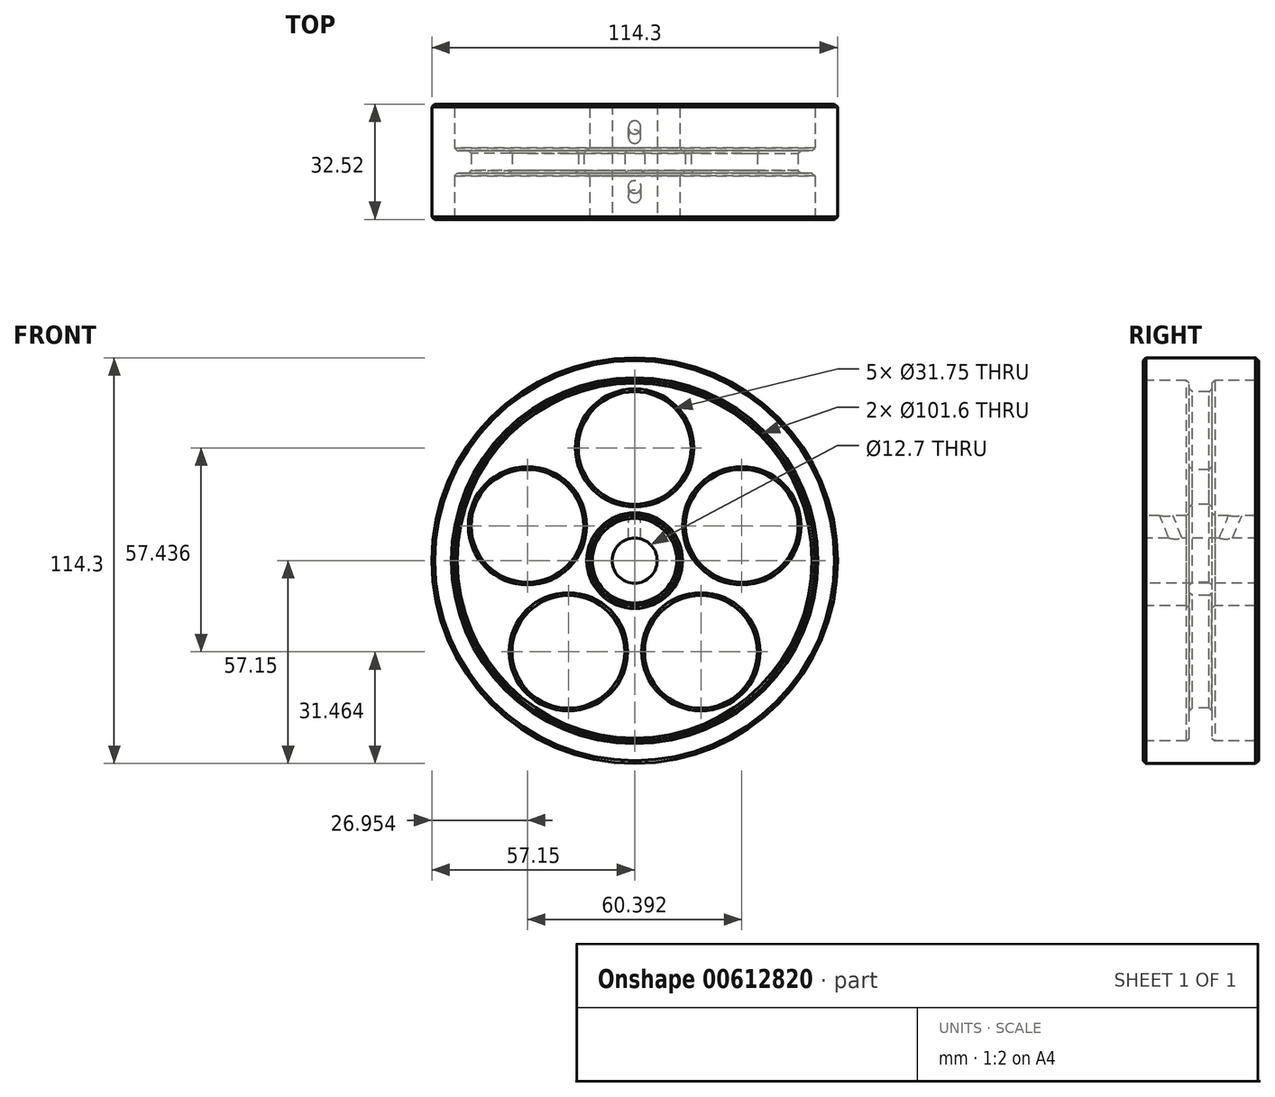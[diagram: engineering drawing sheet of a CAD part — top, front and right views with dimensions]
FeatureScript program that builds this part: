
annotation { "Feature Type Name" : "Feature", "Feature Type Description" : "" }
export const myFeature = defineFeature(function(context is Context, id is Id, definition is map)
    precondition{}
    {
        {
            var Q0;
            Q0=qCreatedBy(makeId("Right.planeOp"),FACE);
            var sketch = newSketch(context, id + "F0", { "sketchPlane" : qUnion([Q0])});
            skLineSegment(sketch, "E0", {"start": v(-16.26, 6.35) * mm, "end": v(-16.26, 12.7) * mm});
            skLineSegment(sketch, "E1", {"start": v(-16.26, 12.7) * mm, "end": v(-3.17, 12.7) * mm});
            skLineSegment(sketch, "E2", {"start": v(-3.17, 12.7) * mm, "end": v(-3.18, 50.8) * mm});
            skLineSegment(sketch, "E3", {"start": v(-3.18, 50.8) * mm, "end": v(-16.26, 50.8) * mm});
            skLineSegment(sketch, "E4", {"start": v(-16.26, 50.8) * mm, "end": v(-16.26, 57.15) * mm});
            skLineSegment(sketch, "E5", {"start": v(-16.26, 57.15) * mm, "end": v(16.26, 57.15) * mm});
            skLineSegment(sketch, "E6", {"start": v(16.26, 57.15) * mm, "end": v(16.26, 50.8) * mm});
            skLineSegment(sketch, "E7", {"start": v(16.26, 50.8) * mm, "end": v(3.17, 50.8) * mm});
            skLineSegment(sketch, "E8", {"start": v(3.17, 50.8) * mm, "end": v(3.18, 12.7) * mm});
            skLineSegment(sketch, "E9", {"start": v(3.18, 12.7) * mm, "end": v(16.26, 12.7) * mm});
            skLineSegment(sketch, "E10", {"start": v(16.26, 12.7) * mm, "end": v(16.26, 6.35) * mm});
            skLineSegment(sketch, "E11", {"start": v(16.26, 6.35) * mm, "end": v(-16.26, 6.35) * mm});
            skLineSegment(sketch, "E12", {"start": v(-16.39, 0) * mm, "end": v(18.55, 0) * mm, "construction": true});
            skPoint(sketch, "E13", {"position": v(0, 57.15) * mm});
            skPoint(sketch, "E14", {"position": v(-9.72, 12.7) * mm});
            skPoint(sketch, "E15", {"position": v(9.72, 12.7) * mm});
            skSolve(sketch);
        }
        {
            var Q0;
            Q0=qSketchRegion(id+"F0",true);
            var Q1;
            Q1=sQuery(id+"F0.wireOp",EDGE,"E12");
            revolve(context, id + "F1", {"entities" : qUnion([Q0]), "axis" : qUnion([Q1]), "revolveType" : RevolveType.FULL});
        }
        {
            var Q0;
            Q0=qCreatedBy(makeId("Front.planeOp"),FACE);
            var sketch = newSketch(context, id + "F2", { "sketchPlane" : qUnion([Q0])});
            skCircle(sketch, "E16", {"center": v(0, 31.75) * mm, "radius": 15.88 * mm});
            skCircle(sketch, "E17.1.0", {"center": v(-30.2, 9.81) * mm, "radius": 15.88 * mm});
            skCircle(sketch, "E17.2.0", {"center": v(-18.66, -25.69) * mm, "radius": 15.88 * mm});
            skCircle(sketch, "E17.3.0", {"center": v(18.66, -25.69) * mm, "radius": 15.88 * mm});
            skCircle(sketch, "E17.4.0", {"center": v(30.2, 9.81) * mm, "radius": 15.88 * mm});
            skPoint(sketch, "E17.center", {"position": v(0, 0) * mm});
            skCircle(sketch, "E18", {"center": v(0, 0) * mm, "radius": 31.75 * mm, "construction": true});
            skSolve(sketch);
        }
        {
            var Q0;
            Q0=qSketchRegion(id+"F2",true);
            extrude(context, id + "F3", {"entities" : qUnion([Q0]), "operationType" : NewBodyOperationType.REMOVE, "oppositeDirection" : true, "depth" : 50.8 * mm, "symmetric" : true});
        }
        {
            var Q0;
            Q0=qCreatedBy(makeId("Top.planeOp"),FACE);
            var sketch = newSketch(context, id + "F4", { "sketchPlane" : qUnion([Q0])});
            skLineSegment(sketch, "E19", {"start": v(-62.2, -50.8) * mm, "end": v(72.14, -50.8) * mm, "construction": true});
            skLineSegment(sketch, "E20", {"start": v(-62.2, 50.8) * mm, "end": v(72.14, 50.8) * mm, "construction": true});
            skSolve(sketch);
        }
        {
            var Q0;
            Q0=sQuery(id+"F4.wireOp",EDGE,"E19");
            cPlane(context, id + "F5", {"entities" : qUnion([Q0]), "cplaneType" : CPlaneType.LINE_ANGLE, "offset" : 152.4 * mm, "angle" : 292.5 * degree, "width" : 152.4 * mm, "height" : 152.4 * mm});
        }
        {
            var Q0;
            Q0=sQuery(id+"F4.wireOp",EDGE,"E20");
            cPlane(context, id + "F6", {"entities" : qUnion([Q0]), "cplaneType" : CPlaneType.LINE_ANGLE, "offset" : 152.4 * mm, "angle" : 67.5 * degree, "width" : 152.4 * mm, "height" : 152.4 * mm});
        }
        {
            var Q0;
            Q0=qCreatedBy(id+"F5.planeOp",FACE);
            var sketch = newSketch(context, id + "F7", { "sketchPlane" : qUnion([Q0])});
            skCircle(sketch, "E21", {"center": v(0, 4.12) * mm, "radius": 1.73 * mm});
            skSolve(sketch);
        }
        {
            var Q0;
            Q0=qSketchRegion(id+"F7",true);
            var Q1;
            Q1=makeQuery(id+"F1.opRevolve","SWEPT_FACE",FACE,{"disambiguationData":[OSD([sQuery(id+"F0.wireOp",EDGE,"E11")])]});
            extrude(context, id + "F8", {"entities" : qUnion([Q0]), "operationType" : NewBodyOperationType.REMOVE, "endBound" : BoundingType.UP_TO_SURFACE, "endBoundEntityFace" : qUnion([Q1]), "depth" : 25.4 * mm});
        }
        {
            var Q0;
            Q0=qCreatedBy(id+"F6.planeOp",FACE);
            var sketch = newSketch(context, id + "F9", { "sketchPlane" : qUnion([Q0])});
            skCircle(sketch, "E22", {"center": v(0, 4.12) * mm, "radius": 1.73 * mm});
            skSolve(sketch);
        }
        {
            var Q0;
            Q0=qSketchRegion(id+"F9",true);
            var Q1;
            Q1=makeQuery(id+"F1.opRevolve","SWEPT_FACE",FACE,{"disambiguationData":[OSD([sQuery(id+"F0.wireOp",EDGE,"E11")])]});
            extrude(context, id + "F10", {"entities" : qUnion([Q0]), "operationType" : NewBodyOperationType.REMOVE, "endBound" : BoundingType.UP_TO_SURFACE, "oppositeDirection" : true, "endBoundEntityFace" : qUnion([Q1]), "depth" : 25.4 * mm});
        }
        {
            var Q0;
            Q0=makeQuery(id+"F1.opRevolve","SWEPT_EDGE",EDGE,{"disambiguationData":[OSD([sQuery(id+"F0.wireOp",EDGE,"E4"),sQuery(id+"F0.wireOp",EDGE,"E5")])]});
            var Q1;
            Q1=makeQuery(id+"F1.opRevolve","SWEPT_EDGE",EDGE,{"disambiguationData":[OSD([sQuery(id+"F0.wireOp",EDGE,"E5"),sQuery(id+"F0.wireOp",EDGE,"E6")])]});
            var Q2;
            Q2=makeQuery(id+"F1.opRevolve","SWEPT_EDGE",EDGE,{"disambiguationData":[OSD([sQuery(id+"F0.wireOp",EDGE,"E3"),sQuery(id+"F0.wireOp",EDGE,"E4")])]});
            var Q3;
            Q3=makeQuery(id+"F1.opRevolve","SWEPT_EDGE",EDGE,{"disambiguationData":[OSD([sQuery(id+"F0.wireOp",EDGE,"E2"),sQuery(id+"F0.wireOp",EDGE,"E3")])]});
            var Q4;
            Q4=makeQuery(id+"F1.opRevolve","SWEPT_EDGE",EDGE,{"disambiguationData":[OSD([sQuery(id+"F0.wireOp",EDGE,"E6"),sQuery(id+"F0.wireOp",EDGE,"E7")])]});
            var Q5;
            Q5=makeQuery(id+"F1.opRevolve","SWEPT_EDGE",EDGE,{"disambiguationData":[OSD([sQuery(id+"F0.wireOp",EDGE,"E7"),sQuery(id+"F0.wireOp",EDGE,"E8")])]});
            var Q6;
            Q6=makeQuery(id+"F1.opRevolve","SWEPT_EDGE",EDGE,{"disambiguationData":[OSD([sQuery(id+"F0.wireOp",EDGE,"E9"),sQuery(id+"F0.wireOp",EDGE,"E10")])]});
            var Q7;
            Q7=makeQuery(id+"F1.opRevolve","SWEPT_EDGE",EDGE,{"disambiguationData":[OSD([sQuery(id+"F0.wireOp",EDGE,"E8"),sQuery(id+"F0.wireOp",EDGE,"E9")])]});
            var Q8;
            Q8=makeQuery(id+"F1.opRevolve","SWEPT_EDGE",EDGE,{"disambiguationData":[OSD([sQuery(id+"F0.wireOp",EDGE,"E0"),sQuery(id+"F0.wireOp",EDGE,"E1")])]});
            var Q9;
            Q9=makeQuery(id+"F1.opRevolve","SWEPT_EDGE",EDGE,{"disambiguationData":[OSD([sQuery(id+"F0.wireOp",EDGE,"E1"),sQuery(id+"F0.wireOp",EDGE,"E2")])]});
            var Q10;
            Q10=makeQuery(id+"F3.boolean.opBoolean","INTERSECT",EDGE,{"derivedFrom":[makeQuery(id+"F1.opRevolve","SWEPT_FACE",FACE,{"disambiguationData":[OSD([sQuery(id+"F0.wireOp",EDGE,"E2")])]}),makeQuery(id+"F3.opExtrude","SWEPT_FACE",FACE,{"disambiguationData":[OSD([sQuery(id+"F2.wireOp",EDGE,"E16")])]})]});
            var Q11;
            Q11=makeQuery(id+"F3.boolean.opBoolean","INTERSECT",EDGE,{"derivedFrom":[makeQuery(id+"F1.opRevolve","SWEPT_FACE",FACE,{"disambiguationData":[OSD([sQuery(id+"F0.wireOp",EDGE,"E2")])]}),makeQuery(id+"F3.opExtrude","SWEPT_FACE",FACE,{"disambiguationData":[OSD([sQuery(id+"F2.wireOp",EDGE,"E17.4.0")])]})]});
            var Q12;
            Q12=makeQuery(id+"F3.boolean.opBoolean","INTERSECT",EDGE,{"derivedFrom":[makeQuery(id+"F1.opRevolve","SWEPT_FACE",FACE,{"disambiguationData":[OSD([sQuery(id+"F0.wireOp",EDGE,"E2")])]}),makeQuery(id+"F3.opExtrude","SWEPT_FACE",FACE,{"disambiguationData":[OSD([sQuery(id+"F2.wireOp",EDGE,"E17.3.0")])]})]});
            var Q13;
            Q13=makeQuery(id+"F3.boolean.opBoolean","INTERSECT",EDGE,{"derivedFrom":[makeQuery(id+"F1.opRevolve","SWEPT_FACE",FACE,{"disambiguationData":[OSD([sQuery(id+"F0.wireOp",EDGE,"E2")])]}),makeQuery(id+"F3.opExtrude","SWEPT_FACE",FACE,{"disambiguationData":[OSD([sQuery(id+"F2.wireOp",EDGE,"E17.2.0")])]})]});
            var Q14;
            Q14=makeQuery(id+"F3.boolean.opBoolean","INTERSECT",EDGE,{"derivedFrom":[makeQuery(id+"F1.opRevolve","SWEPT_FACE",FACE,{"disambiguationData":[OSD([sQuery(id+"F0.wireOp",EDGE,"E2")])]}),makeQuery(id+"F3.opExtrude","SWEPT_FACE",FACE,{"disambiguationData":[OSD([sQuery(id+"F2.wireOp",EDGE,"E17.1.0")])]})]});
            var Q15;
            Q15=makeQuery(id+"F3.boolean.opBoolean","INTERSECT",EDGE,{"derivedFrom":[makeQuery(id+"F1.opRevolve","SWEPT_FACE",FACE,{"disambiguationData":[OSD([sQuery(id+"F0.wireOp",EDGE,"E8")])]}),makeQuery(id+"F3.opExtrude","SWEPT_FACE",FACE,{"disambiguationData":[OSD([sQuery(id+"F2.wireOp",EDGE,"E16")])]})]});
            var Q16;
            Q16=makeQuery(id+"F3.boolean.opBoolean","INTERSECT",EDGE,{"derivedFrom":[makeQuery(id+"F1.opRevolve","SWEPT_FACE",FACE,{"disambiguationData":[OSD([sQuery(id+"F0.wireOp",EDGE,"E8")])]}),makeQuery(id+"F3.opExtrude","SWEPT_FACE",FACE,{"disambiguationData":[OSD([sQuery(id+"F2.wireOp",EDGE,"E17.1.0")])]})]});
            var Q17;
            Q17=makeQuery(id+"F3.boolean.opBoolean","INTERSECT",EDGE,{"derivedFrom":[makeQuery(id+"F1.opRevolve","SWEPT_FACE",FACE,{"disambiguationData":[OSD([sQuery(id+"F0.wireOp",EDGE,"E8")])]}),makeQuery(id+"F3.opExtrude","SWEPT_FACE",FACE,{"disambiguationData":[OSD([sQuery(id+"F2.wireOp",EDGE,"E17.2.0")])]})]});
            var Q18;
            Q18=makeQuery(id+"F3.boolean.opBoolean","INTERSECT",EDGE,{"derivedFrom":[makeQuery(id+"F1.opRevolve","SWEPT_FACE",FACE,{"disambiguationData":[OSD([sQuery(id+"F0.wireOp",EDGE,"E8")])]}),makeQuery(id+"F3.opExtrude","SWEPT_FACE",FACE,{"disambiguationData":[OSD([sQuery(id+"F2.wireOp",EDGE,"E17.3.0")])]})]});
            var Q19;
            Q19=makeQuery(id+"F3.boolean.opBoolean","INTERSECT",EDGE,{"derivedFrom":[makeQuery(id+"F1.opRevolve","SWEPT_FACE",FACE,{"disambiguationData":[OSD([sQuery(id+"F0.wireOp",EDGE,"E8")])]}),makeQuery(id+"F3.opExtrude","SWEPT_FACE",FACE,{"disambiguationData":[OSD([sQuery(id+"F2.wireOp",EDGE,"E17.4.0")])]})]});
            chamfer(context, id + "F11", {"entities" : qUnion([Q0, Q1, Q2, Q3, Q4, Q5, Q6, Q7, Q8, Q9, Q10, Q11, Q12, Q13, Q14, Q15, Q16, Q17, Q18, Q19]), "width" : 0.8 * mm, "tangentPropagation" : true});
        }
    });
